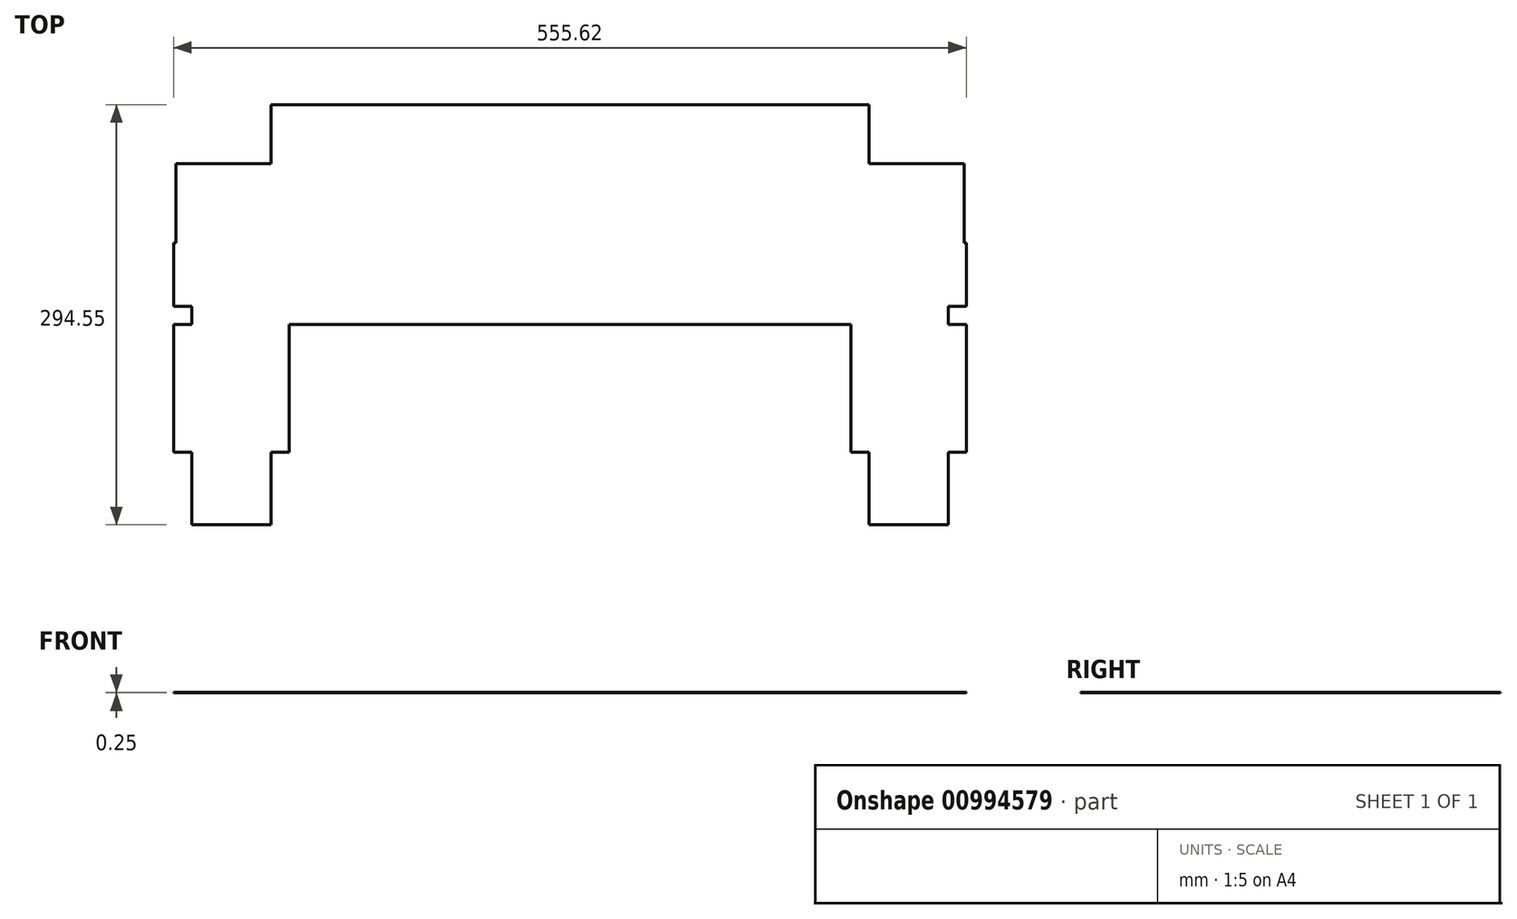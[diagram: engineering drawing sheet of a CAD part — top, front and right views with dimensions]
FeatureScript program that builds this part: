
annotation { "Feature Type Name" : "Feature", "Feature Type Description" : "" }
export const myFeature = defineFeature(function(context is Context, id is Id, definition is map)
    precondition{}
    {
        {
            var Q0;
            Q0=qCreatedBy(makeId("Top.planeOp"),FACE);
            var sketch = newSketch(context, id + "F0", { "sketchPlane" : qUnion([Q0])});
            skLineSegment(sketch, "E0.bottom", {"start": v(0, 0) * mm, "end": v(209.55, 0) * mm, "construction": true});
            skLineSegment(sketch, "E0.top", {"start": v(0, -57.15) * mm, "end": v(209.55, -57.15) * mm});
            skLineSegment(sketch, "E0.left", {"start": v(0, 0) * mm, "end": v(0, -44.45) * mm, "construction": true});
            skLineSegment(sketch, "E1.top", {"start": v(0, 96.84) * mm, "end": v(209.55, 96.84) * mm});
            skLineSegment(sketch, "E1.left", {"start": v(0, 55.56) * mm, "end": v(0, 84.14) * mm});
            skLineSegment(sketch, "E2.bottom", {"start": v(0, 0) * mm, "end": v(-55.56, 0) * mm});
            skLineSegment(sketch, "E3", {"start": v(0, -44.45) * mm, "end": v(209.55, -44.45) * mm, "construction": true});
            skLineSegment(sketch, "E4.top", {"start": v(0, -185.01) * mm, "end": v(-55.56, -185.01) * mm, "construction": true});
            skLineSegment(sketch, "E5", {"start": v(-55.56, -185.01) * mm, "end": v(-55.56, -197.71) * mm});
            skLineSegment(sketch, "E6", {"start": v(-55.56, -197.71) * mm, "end": v(0, -197.71) * mm});
            skLineSegment(sketch, "E7", {"start": v(0, -197.71) * mm, "end": v(0, -185.01) * mm});
            skLineSegment(sketch, "E8", {"start": v(0, -44.45) * mm, "end": v(-55.56, -44.45) * mm, "construction": true});
            skLineSegment(sketch, "E9", {"start": v(0, 0) * mm, "end": v(-66.68, 0) * mm});
            skLineSegment(sketch, "E10", {"start": v(-66.67, 0) * mm, "end": v(-66.67, 55.56) * mm});
            skLineSegment(sketch, "E11", {"start": v(-66.68, 55.56) * mm, "end": v(-53.98, 55.56) * mm});
            skLineSegment(sketch, "E12", {"start": v(-53.98, 55.56) * mm, "end": v(-53.98, 0) * mm, "construction": true});
            skLineSegment(sketch, "E13", {"start": v(-15.88, 55.56) * mm, "end": v(-15.87, 0) * mm, "construction": true});
            skLineSegment(sketch, "E14", {"start": v(0, 84.14) * mm, "end": v(209.55, 84.14) * mm, "construction": true});
            skLineSegment(sketch, "E15", {"start": v(0, 0) * mm, "end": v(0, 55.56) * mm, "construction": true});
            skLineSegment(sketch, "E16", {"start": v(209.55, 55.56) * mm, "end": v(0, 55.56) * mm, "construction": true});
            skLineSegment(sketch, "E17", {"start": v(-55.56, -185.01) * mm, "end": v(-55.56, -57.15) * mm, "construction": true});
            skLineSegment(sketch, "E18", {"start": v(-55.56, 0) * mm, "end": v(-55.56, -44.45) * mm, "construction": true});
            skLineSegment(sketch, "E19", {"start": v(12.7, -146.91) * mm, "end": v(12.7, -57.15) * mm});
            skLineSegment(sketch, "E20", {"start": v(12.7, -57.15) * mm, "end": v(0, -57.15) * mm});
            skLineSegment(sketch, "E21", {"start": v(0, -57.15) * mm, "end": v(0, -146.91) * mm, "construction": true});
            skLineSegment(sketch, "E22", {"start": v(-53.98, 55.56) * mm, "end": v(0, 55.56) * mm});
            skLineSegment(sketch, "E23", {"start": v(-53.98, 0) * mm, "end": v(-53.98, 0) * mm});
            skLineSegment(sketch, "E24", {"start": v(0, 84.14) * mm, "end": v(0, 96.84) * mm});
            skLineSegment(sketch, "E25", {"start": v(0, -44.45) * mm, "end": v(0, -57.15) * mm});
            skLineSegment(sketch, "E26", {"start": v(0, -146.91) * mm, "end": v(12.7, -146.91) * mm});
            skLineSegment(sketch, "E27", {"start": v(97.2, -12.05) * mm, "end": v(93.19, 0) * mm, "construction": true});
            skLineSegment(sketch, "E28", {"start": v(0, -44.45) * mm, "end": v(97.2, -12.05) * mm, "construction": true});
            skLineSegment(sketch, "E29", {"start": v(0, -44.45) * mm, "end": v(12.05, -40.43) * mm, "construction": true});
            skLineSegment(sketch, "E30", {"start": v(-55.56, -146.91) * mm, "end": v(-68.26, -146.91) * mm});
            skLineSegment(sketch, "E31", {"start": v(-55.56, -185.01) * mm, "end": v(-55.56, -146.91) * mm});
            skLineSegment(sketch, "E32", {"start": v(-55.56, -44.45) * mm, "end": v(-68.26, -44.45) * mm});
            skLineSegment(sketch, "E33", {"start": v(-68.26, -44.45) * mm, "end": v(-68.26, 0) * mm});
            skLineSegment(sketch, "E34", {"start": v(-68.26, 0) * mm, "end": v(-55.56, 0) * mm});
            skLineSegment(sketch, "E35", {"start": v(-55.56, -57.15) * mm, "end": v(-68.26, -57.15) * mm});
            skLineSegment(sketch, "E36", {"start": v(-68.26, -57.15) * mm, "end": v(-68.26, -146.91) * mm});
            skLineSegment(sketch, "E37", {"start": v(209.55, -57.15) * mm, "end": v(209.55, 96.84) * mm, "construction": true});
            skLineSegment(sketch, "E38", {"start": v(0, -185.01) * mm, "end": v(0, -146.91) * mm});
            skLineSegment(sketch, "E39", {"start": v(-55.56, -57.15) * mm, "end": v(-55.56, -44.45) * mm});
            skLineSegment(sketch, "E40", {"start": v(-55.56, -185.01) * mm, "end": v(-55.56, -44.45) * mm, "construction": true});
            skLineSegment(sketch, "E41.MirrorCS", {"start": v(419.1, -44.45) * mm, "end": v(419.1, -57.15) * mm});
            skLineSegment(sketch, "E42.MirrorCS", {"start": v(474.66, -57.15) * mm, "end": v(474.66, -44.45) * mm});
            skLineSegment(sketch, "E43.MirrorCS", {"start": v(474.66, -57.15) * mm, "end": v(487.36, -57.15) * mm});
            skLineSegment(sketch, "E44.MirrorCS", {"start": v(406.4, -57.15) * mm, "end": v(419.1, -57.15) * mm});
            skLineSegment(sketch, "E45.MirrorCS", {"start": v(419.1, -146.91) * mm, "end": v(406.4, -146.91) * mm});
            skLineSegment(sketch, "E46.MirrorCS", {"start": v(474.66, -146.91) * mm, "end": v(487.36, -146.91) * mm});
            skLineSegment(sketch, "E47.MirrorCS", {"start": v(419.1, 0) * mm, "end": v(474.66, 0) * mm});
            skLineSegment(sketch, "E48.MirrorCS", {"start": v(419.1, 84.14) * mm, "end": v(419.1, 96.84) * mm});
            skLineSegment(sketch, "E49.MirrorCS", {"start": v(487.36, 0) * mm, "end": v(474.66, 0) * mm});
            skLineSegment(sketch, "E50.MirrorCS", {"start": v(474.66, -185.01) * mm, "end": v(474.66, -146.91) * mm});
            skLineSegment(sketch, "E51.MirrorCS", {"start": v(321.9, -12.05) * mm, "end": v(325.91, 0) * mm, "construction": true});
            skLineSegment(sketch, "E52.MirrorCS", {"start": v(419.1, 0) * mm, "end": v(419.1, -44.45) * mm, "construction": true});
            skLineSegment(sketch, "E53.MirrorCS", {"start": v(474.66, -185.01) * mm, "end": v(474.66, -44.45) * mm, "construction": true});
            skLineSegment(sketch, "E54.MirrorCS", {"start": v(485.78, 55.56) * mm, "end": v(473.08, 55.56) * mm});
            skLineSegment(sketch, "E55.MirrorCS", {"start": v(419.1, -44.45) * mm, "end": v(285.75, 0) * mm, "construction": true});
            skLineSegment(sketch, "E56.MirrorCS", {"start": v(487.36, -44.45) * mm, "end": v(487.36, 0) * mm});
            skLineSegment(sketch, "E57.MirrorCS", {"start": v(473.08, 0) * mm, "end": v(473.08, 0) * mm});
            skLineSegment(sketch, "E58.MirrorCS", {"start": v(474.66, -185.01) * mm, "end": v(474.66, -57.15) * mm, "construction": true});
            skLineSegment(sketch, "E59.MirrorCS", {"start": v(419.1, -197.71) * mm, "end": v(419.1, -185.01) * mm});
            skLineSegment(sketch, "E60.MirrorCS", {"start": v(419.1, 0) * mm, "end": v(209.55, 0) * mm, "construction": true});
            skLineSegment(sketch, "E61.MirrorCS", {"start": v(419.1, -44.45) * mm, "end": v(321.9, -12.05) * mm, "construction": true});
            skLineSegment(sketch, "E62.MirrorCS", {"start": v(419.1, 55.56) * mm, "end": v(419.1, 84.14) * mm});
            skLineSegment(sketch, "E63.MirrorCS", {"start": v(419.1, 0) * mm, "end": v(485.78, 0) * mm});
            skLineSegment(sketch, "E64.MirrorCS", {"start": v(487.36, -57.15) * mm, "end": v(487.36, -146.91) * mm});
            skLineSegment(sketch, "E65.MirrorCS", {"start": v(419.1, -44.45) * mm, "end": v(209.55, -44.45) * mm, "construction": true});
            skLineSegment(sketch, "E66.MirrorCS", {"start": v(419.1, -44.45) * mm, "end": v(474.66, -44.45) * mm, "construction": true});
            skLineSegment(sketch, "E67.MirrorCS", {"start": v(406.4, -146.91) * mm, "end": v(406.4, -57.15) * mm});
            skLineSegment(sketch, "E68.MirrorCS", {"start": v(419.1, -185.01) * mm, "end": v(474.66, -185.01) * mm, "construction": true});
            skLineSegment(sketch, "E69.MirrorCS", {"start": v(473.08, 55.56) * mm, "end": v(473.08, 0) * mm, "construction": true});
            skLineSegment(sketch, "E70.MirrorCS", {"start": v(419.1, 96.84) * mm, "end": v(209.55, 96.84) * mm});
            skLineSegment(sketch, "E71.MirrorCS", {"start": v(209.55, 55.56) * mm, "end": v(419.1, 55.56) * mm, "construction": true});
            skLineSegment(sketch, "E72.MirrorCS", {"start": v(419.1, 84.14) * mm, "end": v(209.55, 84.14) * mm, "construction": true});
            skLineSegment(sketch, "E73.MirrorCS", {"start": v(474.66, -44.45) * mm, "end": v(487.36, -44.45) * mm});
            skLineSegment(sketch, "E74.MirrorCS", {"start": v(419.1, -185.01) * mm, "end": v(419.1, -146.91) * mm});
            skLineSegment(sketch, "E75.MirrorCS", {"start": v(419.1, -57.15) * mm, "end": v(209.55, -57.15) * mm});
            skLineSegment(sketch, "E76.MirrorCS", {"start": v(485.78, 0) * mm, "end": v(485.77, 55.56) * mm});
            skLineSegment(sketch, "E77.MirrorCS", {"start": v(419.1, -57.15) * mm, "end": v(419.1, -146.91) * mm, "construction": true});
            skLineSegment(sketch, "E78.MirrorCS", {"start": v(474.66, -197.71) * mm, "end": v(419.1, -197.71) * mm});
            skLineSegment(sketch, "E79.MirrorCS", {"start": v(474.66, 0) * mm, "end": v(474.66, -44.45) * mm, "construction": true});
            skLineSegment(sketch, "E80.MirrorCS", {"start": v(473.08, 55.56) * mm, "end": v(419.1, 55.56) * mm});
            skLineSegment(sketch, "E81.MirrorCS", {"start": v(474.66, -185.01) * mm, "end": v(474.66, -197.71) * mm});
            skLineSegment(sketch, "E82.MirrorCS", {"start": v(434.98, 55.56) * mm, "end": v(434.98, 0) * mm, "construction": true});
            skLineSegment(sketch, "E83.MirrorCS", {"start": v(419.1, 0) * mm, "end": v(419.1, 55.56) * mm, "construction": true});
            skLineSegment(sketch, "E84", {"start": v(12.05, -40.43) * mm, "end": v(8.03, -28.39) * mm, "construction": true});
            skLineSegment(sketch, "E85", {"start": v(0, -44.45) * mm, "end": v(12.05, -40.43) * mm});
            skLineSegment(sketch, "E86", {"start": v(12.05, -40.43) * mm, "end": v(133.35, 0) * mm, "construction": true});
            skLineSegment(sketch, "E87", {"start": v(8.03, -28.39) * mm, "end": v(93.19, 0) * mm, "construction": true});
            skLineSegment(sketch, "E88", {"start": v(-55.56, -44.45) * mm, "end": v(-55.56, -185.01) * mm});
            skSolve(sketch);
        }
        {
            var Q0;
            Q0 = qSketchRegion(id + "F0", true);
            var Q1;
            Q1 = qConstructionFilter(qBodyType(qCreatedBy(id + "F0" ,EDGE), BodyType.WIRE), ConstructionObject.NO);
            extrude(context, id + "F1", {"entities" : qUnion([Q0]), "surfaceEntities" : qUnion([Q1]), "oppositeDirection" : true, "depth" : 0.25 * mm, "offsetDistance" : 25.4 * mm});
        }
    });
